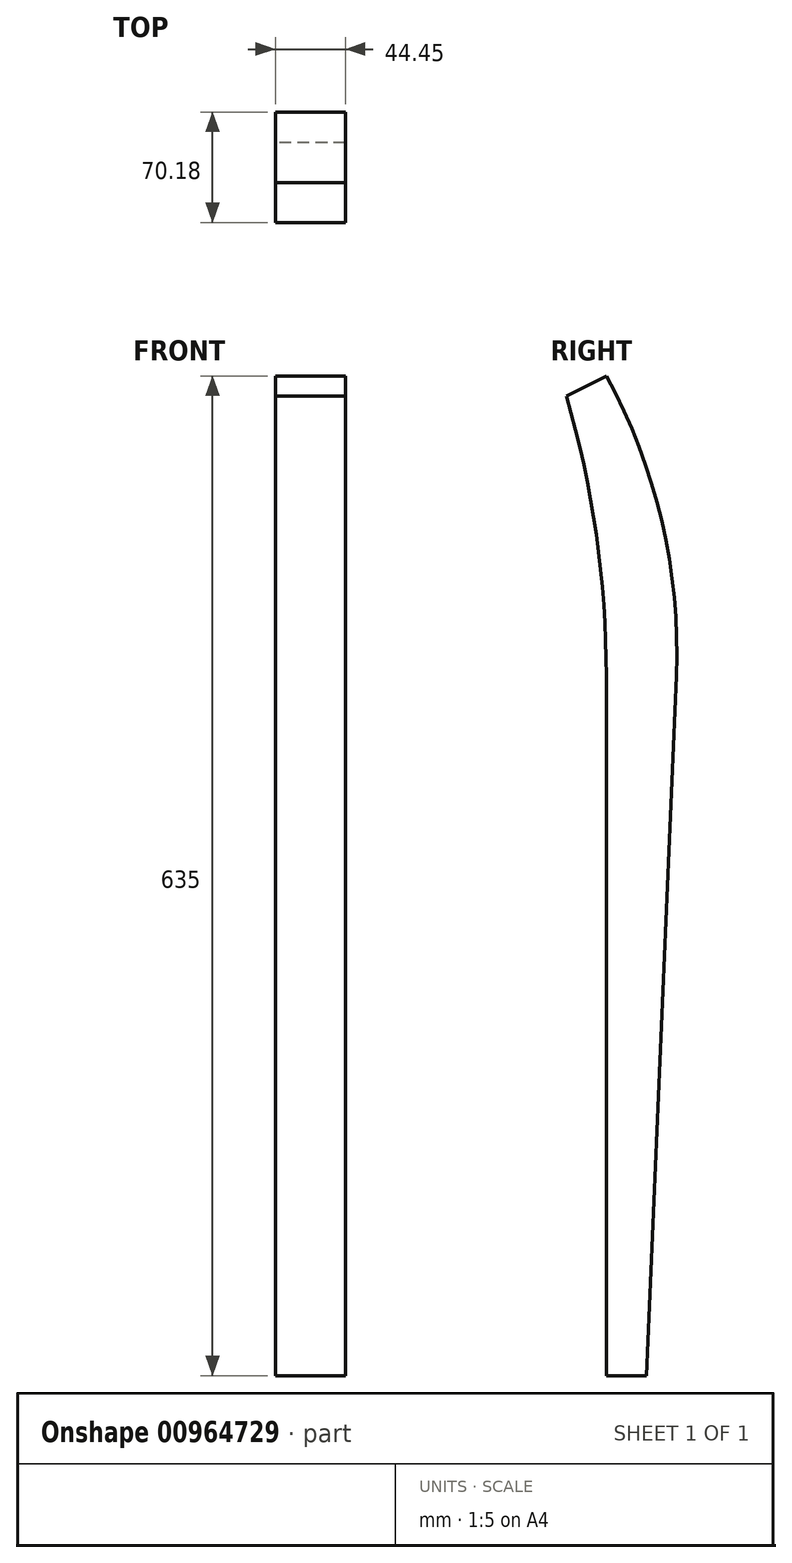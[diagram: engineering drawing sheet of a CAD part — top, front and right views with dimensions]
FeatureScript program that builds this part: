
annotation { "Feature Type Name" : "Feature", "Feature Type Description" : "" }
export const myFeature = defineFeature(function(context is Context, id is Id, definition is map)
    precondition{}
    {
        {
            var Q0;
            Q0=qCreatedBy(makeId("Right.planeOp"),FACE);
            var sketch = newSketch(context, id + "F0", { "sketchPlane" : qUnion([Q0])});
            skLineSegment(sketch, "E0", {"start": v(25.4, 0) * mm, "end": v(0, 0) * mm});
            skLineSegment(sketch, "E1", {"start": v(25.4, 0) * mm, "end": v(44.45, 444.5) * mm});
            skLineSegment(sketch, "E2", {"start": v(0, 0) * mm, "end": v(0, 444.5) * mm});
            skLineSegment(sketch, "E3", {"start": v(-25.4, 622.3) * mm, "end": v(0, 635) * mm});
            skArc(sketch, "E4", {"start": v(44.45, 444.5) * mm, "mid": v(35.26, 542.8) * mm, "end": v(0, 635) * mm});
            skArc(sketch, "E5", {"start": v(0, 444.5) * mm, "mid": v(-6.38, 534.3) * mm, "end": v(-25.4, 622.3) * mm});
            skSolve(sketch);
        }
        {
            var Q0;
            Q0 = qSketchRegion(id + "F0", true);
            extrude(context, id + "F1", {"entities" : qUnion([Q0]), "depth" : 44.45 * mm, "offsetDistance" : 25.4 * mm});
        }
    });
